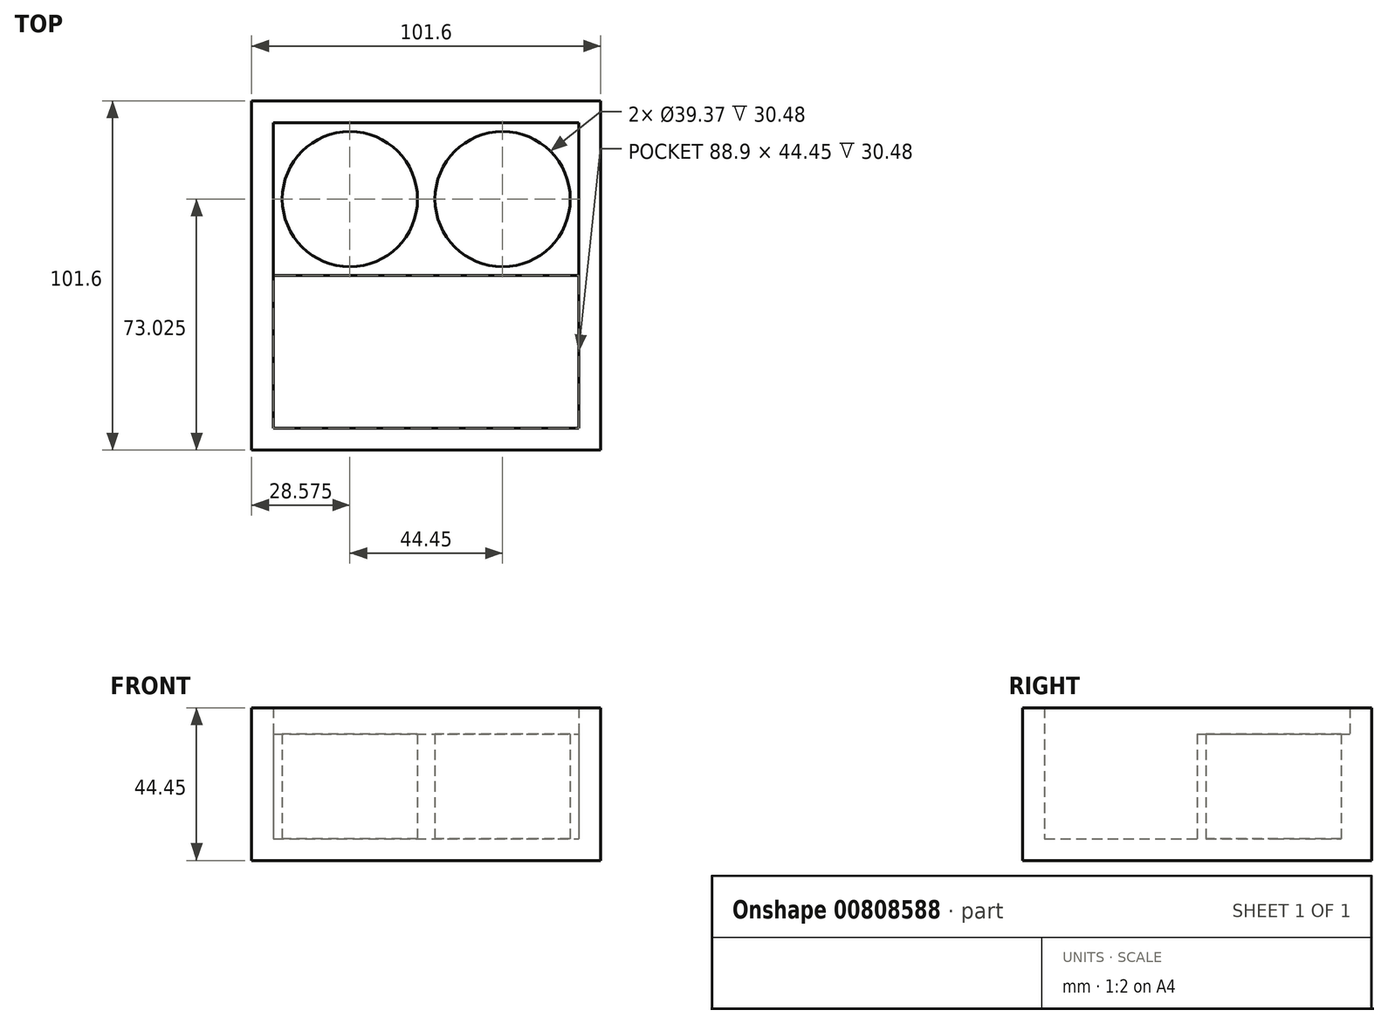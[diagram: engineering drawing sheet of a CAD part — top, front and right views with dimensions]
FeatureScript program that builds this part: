
annotation { "Feature Type Name" : "Feature", "Feature Type Description" : "" }
export const myFeature = defineFeature(function(context is Context, id is Id, definition is map)
    precondition{}
    {
        {
            var Q0;
            Q0=qCreatedBy(makeId("Top.planeOp"),FACE);
            var sketch = newSketch(context, id + "F0", { "sketchPlane" : qUnion([Q0])});
            skLineSegment(sketch, "E0.bottom", {"start": v(50.8, 50.8) * mm, "end": v(-50.8, 50.8) * mm});
            skLineSegment(sketch, "E0.top", {"start": v(50.8, -50.8) * mm, "end": v(-50.8, -50.8) * mm});
            skLineSegment(sketch, "E0.left", {"start": v(50.8, 50.8) * mm, "end": v(50.8, -50.8) * mm});
            skLineSegment(sketch, "E0.right", {"start": v(-50.8, 50.8) * mm, "end": v(-50.8, -50.8) * mm});
            skPoint(sketch, "E0.middle", {"position": v(0, 0) * mm});
            skSolve(sketch);
        }
        {
            var Q0;
            Q0=makeQuery(id+"F0.imprint","IMPRINT",FACE,{"disambiguationData":[TD([[makeQuery(id+"F0.imprint","IMPRINT",EDGE,{"derivedFrom":sQuery(id+"F0.wireOp",EDGE,"E0.bottom")}),1.0]])]});
            extrude(context, id + "F1", {"entities" : qUnion([Q0]), "depth" : 6.35 * mm, "offsetDistance" : 25.4 * mm});
        }
        {
            var Q0;
            Q0=makeQuery(id+"F1.opExtrude","CAP_FACE",FACE,{"disambiguationData":[OSD([sQuery(id+"F0.wireOp",EDGE,"E0.bottom"),sQuery(id+"F0.wireOp",EDGE,"E0.top"),sQuery(id+"F0.wireOp",EDGE,"E0.left"),sQuery(id+"F0.wireOp",EDGE,"E0.right")])],"isStart":false});
            var sketch = newSketch(context, id + "F2", { "sketchPlane" : qUnion([Q0])});
            skLineSegment(sketch, "E1.bottom", {"start": v(-50.8, 50.8) * mm, "end": v(50.8, 50.8) * mm});
            skLineSegment(sketch, "E1.top", {"start": v(-50.8, 44.45) * mm, "end": v(50.8, 44.45) * mm});
            skLineSegment(sketch, "E1.left", {"start": v(-50.8, 50.8) * mm, "end": v(-50.8, 44.45) * mm});
            skLineSegment(sketch, "E1.right", {"start": v(50.8, 50.8) * mm, "end": v(50.8, 44.45) * mm});
            skLineSegment(sketch, "E2.bottom", {"start": v(50.8, 44.45) * mm, "end": v(44.45, 44.45) * mm});
            skLineSegment(sketch, "E2.top", {"start": v(50.8, -50.8) * mm, "end": v(44.45, -50.8) * mm});
            skLineSegment(sketch, "E2.left", {"start": v(50.8, 44.45) * mm, "end": v(50.8, -50.8) * mm});
            skLineSegment(sketch, "E2.right", {"start": v(44.45, 44.45) * mm, "end": v(44.45, -50.8) * mm});
            skLineSegment(sketch, "E3.bottom", {"start": v(44.45, -50.8) * mm, "end": v(-50.8, -50.8) * mm});
            skLineSegment(sketch, "E3.top", {"start": v(44.45, -44.45) * mm, "end": v(-50.8, -44.45) * mm});
            skLineSegment(sketch, "E3.left", {"start": v(44.45, -50.8) * mm, "end": v(44.45, -44.45) * mm});
            skLineSegment(sketch, "E3.right", {"start": v(-50.8, -50.8) * mm, "end": v(-50.8, -44.45) * mm});
            skLineSegment(sketch, "E4.bottom", {"start": v(-50.8, -44.45) * mm, "end": v(-44.45, -44.45) * mm});
            skLineSegment(sketch, "E4.top", {"start": v(-50.8, 44.45) * mm, "end": v(-44.45, 44.45) * mm});
            skLineSegment(sketch, "E4.left", {"start": v(-50.8, -44.45) * mm, "end": v(-50.8, 44.45) * mm});
            skLineSegment(sketch, "E4.right", {"start": v(-44.45, -44.45) * mm, "end": v(-44.45, 44.45) * mm});
            skSolve(sketch);
        }
        {
            var Q0;
            Q0 = qSketchRegion(id + "F2", true);
            extrude(context, id + "F3", {"entities" : qUnion([Q0]), "operationType" : NewBodyOperationType.ADD, "depth" : 38.1 * mm, "offsetDistance" : 25.4 * mm});
        }
        {
            var Q0;
            Q0=makeQuery(id+"F1.opExtrude","CAP_FACE",FACE,{"disambiguationData":[OSD([sQuery(id+"F0.wireOp",EDGE,"E0.bottom"),sQuery(id+"F0.wireOp",EDGE,"E0.top"),sQuery(id+"F0.wireOp",EDGE,"E0.left"),sQuery(id+"F0.wireOp",EDGE,"E0.right")])],"isStart":false});
            var sketch = newSketch(context, id + "F4", { "sketchPlane" : qUnion([Q0])});
            skLineSegment(sketch, "E5", {"start": v(0, 44.45) * mm, "end": v(0, -44.45) * mm});
            skLineSegment(sketch, "E6", {"start": v(-44.45, 0) * mm, "end": v(44.45, 0) * mm});
            skLineSegment(sketch, "E7", {"start": v(0, 0) * mm, "end": v(-44.45, 0) * mm});
            skLineSegment(sketch, "E8", {"start": v(0, 0) * mm, "end": v(44.45, 0) * mm});
            skLineSegment(sketch, "E9", {"start": v(0, 0) * mm, "end": v(0, 44.45) * mm});
            skLineSegment(sketch, "E10", {"start": v(0, 0) * mm, "end": v(0, -44.45) * mm});
            skLineSegment(sketch, "E11.bottom", {"start": v(-44.45, 44.45) * mm, "end": v(0, 44.45) * mm});
            skLineSegment(sketch, "E11.top", {"start": v(-44.45, 0) * mm, "end": v(0, 0) * mm});
            skLineSegment(sketch, "E11.left", {"start": v(-44.45, 44.45) * mm, "end": v(-44.45, 0) * mm});
            skLineSegment(sketch, "E11.right", {"start": v(0, 44.45) * mm, "end": v(0, 0) * mm});
            skLineSegment(sketch, "E12.top", {"start": v(0, 44.45) * mm, "end": v(44.45, 44.45) * mm});
            skLineSegment(sketch, "E12.right", {"start": v(44.45, 0) * mm, "end": v(44.45, 44.45) * mm});
            skLineSegment(sketch, "E13.top", {"start": v(0, -44.45) * mm, "end": v(44.45, -44.45) * mm});
            skLineSegment(sketch, "E13.right", {"start": v(44.45, 0) * mm, "end": v(44.45, -44.45) * mm});
            skLineSegment(sketch, "E14.top", {"start": v(0, -44.45) * mm, "end": v(-44.45, -44.45) * mm});
            skLineSegment(sketch, "E14.right", {"start": v(-44.45, 0) * mm, "end": v(-44.45, -44.45) * mm});
            skCircle(sketch, "E15", {"center": v(-22.23, -22.23) * mm, "radius": 19.69 * mm});
            skPoint(sketch, "E15.centerSnap0", {"position": v(0, -22.23) * mm});
            skPoint(sketch, "E15.centerSnap1", {"position": v(-22.23, 0) * mm});
            skCircle(sketch, "E16", {"center": v(-22.23, 22.23) * mm, "radius": 19.69 * mm});
            skPoint(sketch, "E16.centerSnap0", {"position": v(0, 22.22) * mm});
            skCircle(sketch, "E17", {"center": v(22.23, 22.23) * mm, "radius": 19.69 * mm});
            skPoint(sketch, "E17.centerSnap0", {"position": v(22.23, 0) * mm});
            skCircle(sketch, "E18", {"center": v(22.23, -22.23) * mm, "radius": 19.69 * mm});
            skSolve(sketch);
        }
        {
            var Q0;
            Q0=makeQuery(id+"F4.imprint","IMPRINT",FACE,{"disambiguationData":[TD([[makeQuery(id+"F4.imprint","IMPRINT",EDGE,{"derivedFrom":sQuery(id+"F4.wireOp",EDGE,"E11.bottom")}),-1.0]])]});
            var Q1;
            Q1=makeQuery(id+"F4.imprint","IMPRINT",FACE,{"disambiguationData":[TD([[makeQuery(id+"F4.imprint","IMPRINT",EDGE,{"derivedFrom":sQuery(id+"F4.wireOp",EDGE,"E12.top")}),-1.0]])]});
            var Q2;
            Q2=makeQuery(id+"F4.imprint","IMPRINT",FACE,{"disambiguationData":[TD([[makeQuery(id+"F4.imprint","IMPRINT",EDGE,{"derivedFrom":sQuery(id+"F4.wireOp",EDGE,"E8")}),-1.0]])]});
            var Q3;
            Q3=makeQuery(id+"F4.imprint","IMPRINT",FACE,{"disambiguationData":[TD([[makeQuery(id+"F4.imprint","IMPRINT",EDGE,{"derivedFrom":sQuery(id+"F4.wireOp",EDGE,"E7")}),1.0]])]});
            extrude(context, id + "F5", {"entities" : qUnion([Q0, Q1, Q2, Q3]), "operationType" : NewBodyOperationType.ADD, "depth" : 30.48 * mm, "offsetDistance" : 25.4 * mm});
        }
    });
